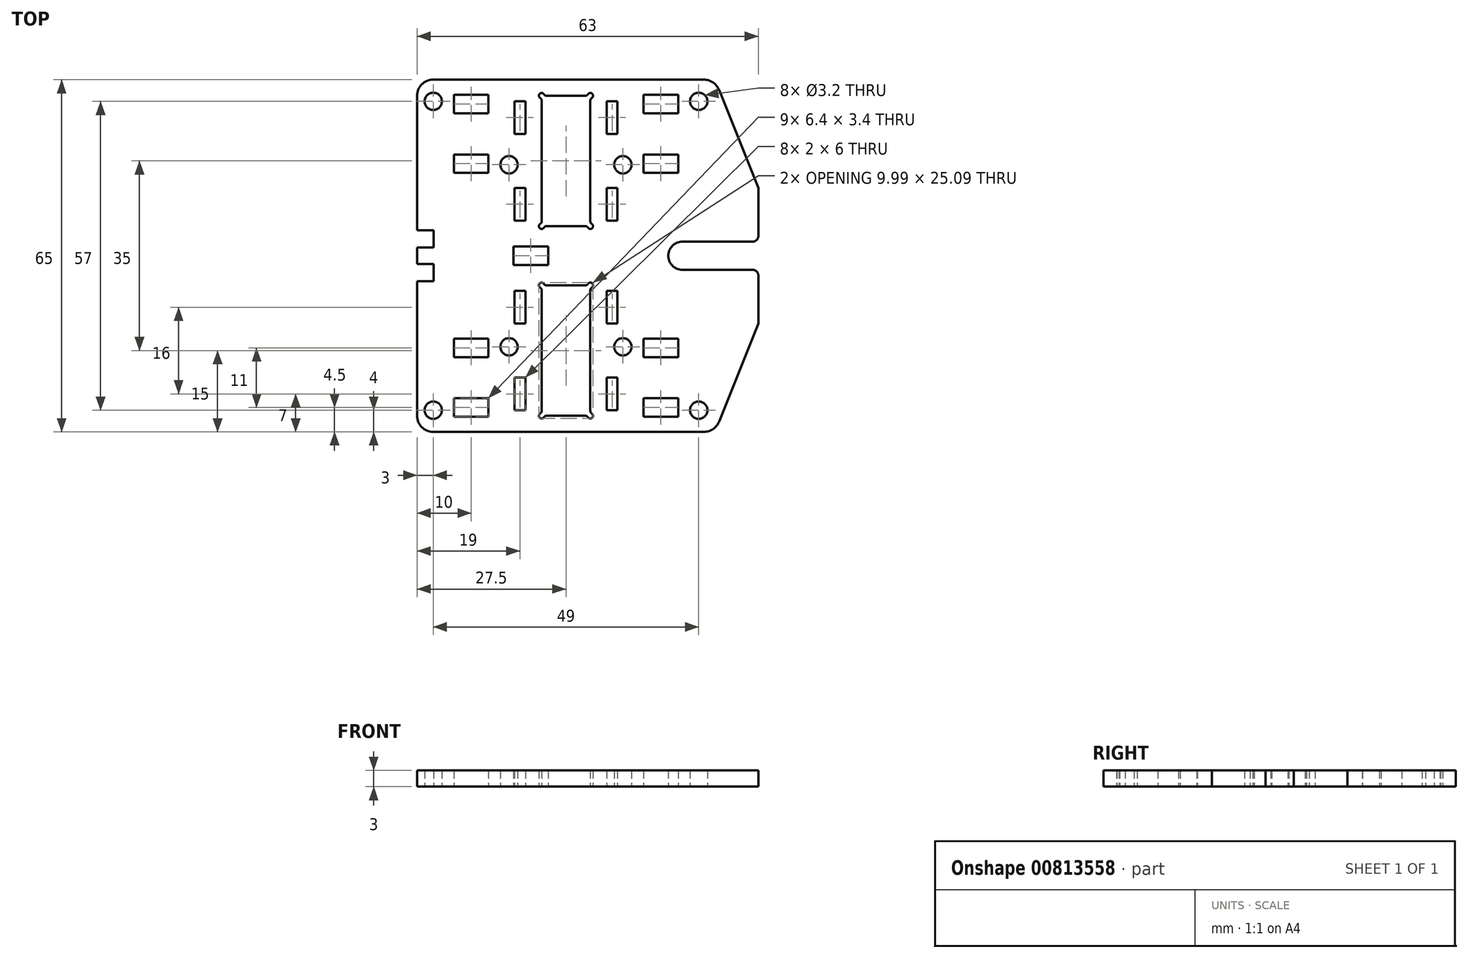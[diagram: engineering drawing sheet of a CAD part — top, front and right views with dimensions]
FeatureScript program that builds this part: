
annotation { "Feature Type Name" : "Feature", "Feature Type Description" : "" }
export const myFeature = defineFeature(function(context is Context, id is Id, definition is map)
    precondition{}
    {
        {
            var Q0;
            Q0=qCreatedBy(makeId("Top.planeOp"),FACE);
            var sketch = newSketch(context, id + "F0", { "sketchPlane" : qUnion([Q0])});
            skLineSegment(sketch, "E0", {"start": v(-31.5, -1.5) * mm, "end": v(-31.5, 1.5) * mm});
            skArc(sketch, "E1", {"start": v(-8.75, -29.12) * mm, "mid": v(-8.85, -29.9) * mm, "end": v(-8.07, -29.8) * mm});
            skArc(sketch, "E2", {"start": v(-7.63, -29.55) * mm, "mid": v(-7.88, -29.62) * mm, "end": v(-8.07, -29.8) * mm});
            skArc(sketch, "E3", {"start": v(-8.75, -29.12) * mm, "mid": v(-8.57, -28.93) * mm, "end": v(-8.5, -28.68) * mm});
            skLineSegment(sketch, "E4", {"start": v(-8.5, -6.32) * mm, "end": v(-8.5, -28.68) * mm});
            skArc(sketch, "E5", {"start": v(-8.5, -6.32) * mm, "mid": v(-8.57, -6.07) * mm, "end": v(-8.75, -5.88) * mm});
            skArc(sketch, "E6", {"start": v(-8.07, -5.2) * mm, "mid": v(-8.85, -5.1) * mm, "end": v(-8.75, -5.88) * mm});
            skArc(sketch, "E7", {"start": v(-8.07, -5.2) * mm, "mid": v(-7.88, -5.38) * mm, "end": v(-7.63, -5.45) * mm});
            skLineSegment(sketch, "E8", {"start": v(-0.37, -5.45) * mm, "end": v(-7.63, -5.45) * mm});
            skArc(sketch, "E9", {"start": v(-0.37, -5.45) * mm, "mid": v(-0.12, -5.38) * mm, "end": v(0.07, -5.2) * mm});
            skArc(sketch, "E10", {"start": v(0.75, -5.88) * mm, "mid": v(0.85, -5.1) * mm, "end": v(0.07, -5.2) * mm});
            skArc(sketch, "E11", {"start": v(0.75, -5.88) * mm, "mid": v(0.57, -6.07) * mm, "end": v(0.5, -6.32) * mm});
            skLineSegment(sketch, "E12", {"start": v(0.5, -28.68) * mm, "end": v(0.5, -6.32) * mm});
            skArc(sketch, "E13", {"start": v(0.5, -28.68) * mm, "mid": v(0.57, -28.93) * mm, "end": v(0.75, -29.12) * mm});
            skArc(sketch, "E14", {"start": v(0.07, -29.8) * mm, "mid": v(0.85, -29.9) * mm, "end": v(0.75, -29.12) * mm});
            skArc(sketch, "E15", {"start": v(0.07, -29.8) * mm, "mid": v(-0.12, -29.62) * mm, "end": v(-0.37, -29.55) * mm});
            skLineSegment(sketch, "E16", {"start": v(-7.63, -29.55) * mm, "end": v(-0.37, -29.55) * mm});
            skArc(sketch, "E17", {"start": v(-8.75, 5.88) * mm, "mid": v(-8.85, 5.1) * mm, "end": v(-8.07, 5.2) * mm});
            skArc(sketch, "E18", {"start": v(-7.63, 5.45) * mm, "mid": v(-7.88, 5.38) * mm, "end": v(-8.07, 5.2) * mm});
            skArc(sketch, "E19", {"start": v(-8.75, 5.88) * mm, "mid": v(-8.57, 6.07) * mm, "end": v(-8.5, 6.32) * mm});
            skLineSegment(sketch, "E20", {"start": v(-8.5, 28.68) * mm, "end": v(-8.5, 6.32) * mm});
            skArc(sketch, "E21", {"start": v(-8.5, 28.68) * mm, "mid": v(-8.57, 28.93) * mm, "end": v(-8.75, 29.12) * mm});
            skArc(sketch, "E22", {"start": v(-8.07, 29.8) * mm, "mid": v(-8.85, 29.9) * mm, "end": v(-8.75, 29.12) * mm});
            skArc(sketch, "E23", {"start": v(-8.07, 29.8) * mm, "mid": v(-7.88, 29.62) * mm, "end": v(-7.63, 29.55) * mm});
            skLineSegment(sketch, "E24", {"start": v(-0.37, 29.55) * mm, "end": v(-7.63, 29.55) * mm});
            skArc(sketch, "E25", {"start": v(-0.37, 29.55) * mm, "mid": v(-0.12, 29.62) * mm, "end": v(0.07, 29.8) * mm});
            skArc(sketch, "E26", {"start": v(0.75, 29.12) * mm, "mid": v(0.85, 29.9) * mm, "end": v(0.07, 29.8) * mm});
            skArc(sketch, "E27", {"start": v(0.75, 29.12) * mm, "mid": v(0.57, 28.93) * mm, "end": v(0.5, 28.68) * mm});
            skLineSegment(sketch, "E28", {"start": v(0.5, 6.32) * mm, "end": v(0.5, 28.68) * mm});
            skArc(sketch, "E29", {"start": v(0.5, 6.32) * mm, "mid": v(0.57, 6.07) * mm, "end": v(0.75, 5.88) * mm});
            skArc(sketch, "E30", {"start": v(0.07, 5.2) * mm, "mid": v(0.85, 5.1) * mm, "end": v(0.75, 5.88) * mm});
            skArc(sketch, "E31", {"start": v(0.07, 5.2) * mm, "mid": v(-0.12, 5.38) * mm, "end": v(-0.37, 5.45) * mm});
            skLineSegment(sketch, "E32", {"start": v(-7.63, 5.45) * mm, "end": v(-0.37, 5.45) * mm});
            skLineSegment(sketch, "E33", {"start": v(-31.5, -4.7) * mm, "end": v(-28.4, -4.7) * mm});
            skLineSegment(sketch, "E34", {"start": v(-28.4, -1.5) * mm, "end": v(-31.5, -1.5) * mm});
            skLineSegment(sketch, "E35", {"start": v(-28.4, -4.7) * mm, "end": v(-28.4, -1.5) * mm});
            skLineSegment(sketch, "E36", {"start": v(-31.5, 1.5) * mm, "end": v(-28.4, 1.5) * mm});
            skLineSegment(sketch, "E37", {"start": v(-28.4, 4.7) * mm, "end": v(-31.5, 4.7) * mm});
            skLineSegment(sketch, "E38", {"start": v(-28.4, 1.5) * mm, "end": v(-28.4, 4.7) * mm});
            skLineSegment(sketch, "E39", {"start": v(-13.7, 1.7) * mm, "end": v(-13.7, -1.7) * mm});
            skLineSegment(sketch, "E40", {"start": v(-13.7, -1.7) * mm, "end": v(-7.3, -1.7) * mm});
            skLineSegment(sketch, "E41", {"start": v(-13.7, 1.7) * mm, "end": v(-7.3, 1.7) * mm});
            skLineSegment(sketch, "E42", {"start": v(-7.3, -1.7) * mm, "end": v(-7.3, 1.7) * mm});
            skLineSegment(sketch, "E43", {"start": v(3.5, -12.5) * mm, "end": v(5.5, -12.5) * mm});
            skLineSegment(sketch, "E44", {"start": v(-13.5, -12.5) * mm, "end": v(-11.5, -12.5) * mm});
            skLineSegment(sketch, "E45", {"start": v(5.5, 12.5) * mm, "end": v(3.5, 12.5) * mm});
            skLineSegment(sketch, "E46", {"start": v(-11.5, 12.5) * mm, "end": v(-13.5, 12.5) * mm});
            skLineSegment(sketch, "E47", {"start": v(3.5, 22.5) * mm, "end": v(5.5, 22.5) * mm});
            skLineSegment(sketch, "E48", {"start": v(-13.5, 22.5) * mm, "end": v(-11.5, 22.5) * mm});
            skLineSegment(sketch, "E49", {"start": v(5.5, -22.5) * mm, "end": v(3.5, -22.5) * mm});
            skLineSegment(sketch, "E50", {"start": v(-11.5, -22.5) * mm, "end": v(-13.5, -22.5) * mm});
            skLineSegment(sketch, "E51", {"start": v(-13.5, -28.5) * mm, "end": v(-11.5, -28.5) * mm});
            skLineSegment(sketch, "E52", {"start": v(-11.5, -6.5) * mm, "end": v(-13.5, -6.5) * mm});
            skLineSegment(sketch, "E53", {"start": v(-13.5, 6.5) * mm, "end": v(-11.5, 6.5) * mm});
            skLineSegment(sketch, "E54", {"start": v(-11.5, 28.5) * mm, "end": v(-13.5, 28.5) * mm});
            skLineSegment(sketch, "E55", {"start": v(3.5, -28.5) * mm, "end": v(5.5, -28.5) * mm});
            skLineSegment(sketch, "E56", {"start": v(5.5, -6.5) * mm, "end": v(3.5, -6.5) * mm});
            skLineSegment(sketch, "E57", {"start": v(3.5, 6.5) * mm, "end": v(5.5, 6.5) * mm});
            skLineSegment(sketch, "E58", {"start": v(5.5, 28.5) * mm, "end": v(3.5, 28.5) * mm});
            skLineSegment(sketch, "E59", {"start": v(-13.5, -22.5) * mm, "end": v(-13.5, -28.5) * mm});
            skLineSegment(sketch, "E60", {"start": v(-11.5, -28.5) * mm, "end": v(-11.5, -22.5) * mm});
            skLineSegment(sketch, "E61", {"start": v(-13.5, -6.5) * mm, "end": v(-13.5, -12.5) * mm});
            skLineSegment(sketch, "E62", {"start": v(-11.5, -12.5) * mm, "end": v(-11.5, -6.5) * mm});
            skLineSegment(sketch, "E63", {"start": v(-13.5, 12.5) * mm, "end": v(-13.5, 6.5) * mm});
            skLineSegment(sketch, "E64", {"start": v(-11.5, 6.5) * mm, "end": v(-11.5, 12.5) * mm});
            skLineSegment(sketch, "E65", {"start": v(-13.5, 28.5) * mm, "end": v(-13.5, 22.5) * mm});
            skLineSegment(sketch, "E66", {"start": v(-11.5, 22.5) * mm, "end": v(-11.5, 28.5) * mm});
            skLineSegment(sketch, "E67", {"start": v(3.5, -22.5) * mm, "end": v(3.5, -28.5) * mm});
            skLineSegment(sketch, "E68", {"start": v(5.5, -28.5) * mm, "end": v(5.5, -22.5) * mm});
            skLineSegment(sketch, "E69", {"start": v(3.5, -6.5) * mm, "end": v(3.5, -12.5) * mm});
            skLineSegment(sketch, "E70", {"start": v(5.5, -12.5) * mm, "end": v(5.5, -6.5) * mm});
            skLineSegment(sketch, "E71", {"start": v(3.5, 12.5) * mm, "end": v(3.5, 6.5) * mm});
            skLineSegment(sketch, "E72", {"start": v(5.5, 6.5) * mm, "end": v(5.5, 12.5) * mm});
            skLineSegment(sketch, "E73", {"start": v(3.5, 28.5) * mm, "end": v(3.5, 22.5) * mm});
            skLineSegment(sketch, "E74", {"start": v(5.5, 22.5) * mm, "end": v(5.5, 28.5) * mm});
            skArc(sketch, "E75", {"start": v(17.5, 2.6) * mm, "mid": v(14.9, 0) * mm, "end": v(17.5, -2.6) * mm});
            skLineSegment(sketch, "E76", {"start": v(31.5, 12.5) * mm, "end": v(31.5, 3.6) * mm});
            skLineSegment(sketch, "E77", {"start": v(17.5, 2.6) * mm, "end": v(30.5, 2.6) * mm});
            skArc(sketch, "E78", {"start": v(30.5, 2.6) * mm, "mid": v(31.2, 2.9) * mm, "end": v(31.5, 3.6) * mm});
            skLineSegment(sketch, "E79", {"start": v(17.5, -2.6) * mm, "end": v(30.5, -2.6) * mm});
            skLineSegment(sketch, "E80", {"start": v(31.5, -12.5) * mm, "end": v(31.5, -3.6) * mm});
            skArc(sketch, "E81", {"start": v(31.5, -3.6) * mm, "mid": v(31.2, -2.9) * mm, "end": v(30.5, -2.6) * mm});
            skLineSegment(sketch, "E82", {"start": v(10.3, -26.3) * mm, "end": v(10.3, -29.7) * mm});
            skLineSegment(sketch, "E83", {"start": v(10.3, -29.7) * mm, "end": v(16.7, -29.7) * mm});
            skLineSegment(sketch, "E84", {"start": v(10.3, -26.3) * mm, "end": v(16.7, -26.3) * mm});
            skLineSegment(sketch, "E85", {"start": v(16.7, -29.7) * mm, "end": v(16.7, -26.3) * mm});
            skLineSegment(sketch, "E86", {"start": v(10.3, -15.3) * mm, "end": v(10.3, -18.7) * mm});
            skLineSegment(sketch, "E87", {"start": v(10.3, -18.7) * mm, "end": v(16.7, -18.7) * mm});
            skLineSegment(sketch, "E88", {"start": v(10.3, -15.3) * mm, "end": v(16.7, -15.3) * mm});
            skLineSegment(sketch, "E89", {"start": v(16.7, -18.7) * mm, "end": v(16.7, -15.3) * mm});
            skLineSegment(sketch, "E90", {"start": v(10.3, 18.7) * mm, "end": v(10.3, 15.3) * mm});
            skLineSegment(sketch, "E91", {"start": v(10.3, 15.3) * mm, "end": v(16.7, 15.3) * mm});
            skLineSegment(sketch, "E92", {"start": v(10.3, 18.7) * mm, "end": v(16.7, 18.7) * mm});
            skLineSegment(sketch, "E93", {"start": v(16.7, 15.3) * mm, "end": v(16.7, 18.7) * mm});
            skLineSegment(sketch, "E94", {"start": v(10.3, 29.7) * mm, "end": v(10.3, 26.3) * mm});
            skLineSegment(sketch, "E95", {"start": v(10.3, 26.3) * mm, "end": v(16.7, 26.3) * mm});
            skLineSegment(sketch, "E96", {"start": v(10.3, 29.7) * mm, "end": v(16.7, 29.7) * mm});
            skLineSegment(sketch, "E97", {"start": v(16.7, 26.3) * mm, "end": v(16.7, 29.7) * mm});
            skCircle(sketch, "E98", {"center": v(20.5, -28.5) * mm, "radius": 1.6 * mm});
            skCircle(sketch, "E99", {"center": v(20.5, 28.5) * mm, "radius": 1.6 * mm});
            skLineSegment(sketch, "E100", {"start": v(-24.7, -26.3) * mm, "end": v(-24.7, -29.7) * mm});
            skLineSegment(sketch, "E101", {"start": v(-24.7, -29.7) * mm, "end": v(-18.3, -29.7) * mm});
            skLineSegment(sketch, "E102", {"start": v(-24.7, -26.3) * mm, "end": v(-18.3, -26.3) * mm});
            skLineSegment(sketch, "E103", {"start": v(-18.3, -29.7) * mm, "end": v(-18.3, -26.3) * mm});
            skLineSegment(sketch, "E104", {"start": v(-24.7, -15.3) * mm, "end": v(-24.7, -18.7) * mm});
            skLineSegment(sketch, "E105", {"start": v(-24.7, -18.7) * mm, "end": v(-18.3, -18.7) * mm});
            skLineSegment(sketch, "E106", {"start": v(-24.7, -15.3) * mm, "end": v(-18.3, -15.3) * mm});
            skLineSegment(sketch, "E107", {"start": v(-18.3, -18.7) * mm, "end": v(-18.3, -15.3) * mm});
            skLineSegment(sketch, "E108", {"start": v(-24.7, 18.7) * mm, "end": v(-24.7, 15.3) * mm});
            skLineSegment(sketch, "E109", {"start": v(-24.7, 15.3) * mm, "end": v(-18.3, 15.3) * mm});
            skLineSegment(sketch, "E110", {"start": v(-24.7, 18.7) * mm, "end": v(-18.3, 18.7) * mm});
            skLineSegment(sketch, "E111", {"start": v(-18.3, 15.3) * mm, "end": v(-18.3, 18.7) * mm});
            skLineSegment(sketch, "E112", {"start": v(-24.7, 29.7) * mm, "end": v(-24.7, 26.3) * mm});
            skLineSegment(sketch, "E113", {"start": v(-24.7, 26.3) * mm, "end": v(-18.3, 26.3) * mm});
            skLineSegment(sketch, "E114", {"start": v(-24.7, 29.7) * mm, "end": v(-18.3, 29.7) * mm});
            skLineSegment(sketch, "E115", {"start": v(-18.3, 26.3) * mm, "end": v(-18.3, 29.7) * mm});
            skCircle(sketch, "E116", {"center": v(-28.5, -28.5) * mm, "radius": 1.6 * mm});
            skCircle(sketch, "E117", {"center": v(-28.5, 28.5) * mm, "radius": 1.6 * mm});
            skCircle(sketch, "E118", {"center": v(-14.5, -16.8) * mm, "radius": 1.6 * mm});
            skCircle(sketch, "E119", {"center": v(6.5, -16.8) * mm, "radius": 1.6 * mm});
            skCircle(sketch, "E120", {"center": v(6.5, 16.8) * mm, "radius": 1.6 * mm});
            skCircle(sketch, "E121", {"center": v(-14.5, 16.8) * mm, "radius": 1.6 * mm});
            skArc(sketch, "E122", {"start": v(24.25, 30.61) * mm, "mid": v(23.15, 31.98) * mm, "end": v(21.47, 32.5) * mm});
            skLineSegment(sketch, "E123", {"start": v(31.5, -12.5) * mm, "end": v(24.25, -30.61) * mm});
            skArc(sketch, "E124", {"start": v(21.47, -32.5) * mm, "mid": v(23.15, -31.98) * mm, "end": v(24.25, -30.61) * mm});
            skLineSegment(sketch, "E125", {"start": v(-31.5, -29.5) * mm, "end": v(-31.5, -4.7) * mm});
            skLineSegment(sketch, "E126", {"start": v(21.47, -32.5) * mm, "end": v(-28.5, -32.5) * mm});
            skArc(sketch, "E127", {"start": v(-31.5, -29.5) * mm, "mid": v(-30.62, -31.62) * mm, "end": v(-28.5, -32.5) * mm});
            skLineSegment(sketch, "E128", {"start": v(-31.5, 4.7) * mm, "end": v(-31.5, 29.5) * mm});
            skLineSegment(sketch, "E129", {"start": v(21.47, 32.5) * mm, "end": v(-28.5, 32.5) * mm});
            skArc(sketch, "E130", {"start": v(-28.5, 32.5) * mm, "mid": v(-30.62, 31.62) * mm, "end": v(-31.5, 29.5) * mm});
            skLineSegment(sketch, "E131", {"start": v(24.25, 30.61) * mm, "end": v(31.5, 12.5) * mm});
            skSolve(sketch);
        }
        {
            var Q0;
            Q0=qSketchRegion(id+"F0",true);
            extrude(context, id + "F1", {"entities" : qUnion([Q0]), "depth" : 3 * mm, "offsetDistance" : 25 * mm});
        }
        {
            var Q0;
            Q0=makeQuery(id+"F1.opExtrude","CAP_EDGE",EDGE,{"disambiguationData":[OSD([sQuery(id+"F0.wireOp",EDGE,"E20")])],"isStart":false});
            cPoint(context, id + "F2", {"entities" : qUnion([Q0]), "parameter" : 0.5});
        }
        {
            var Q0;
            Q0=qCreatedBy(id+"F2",VERTEX);
            var Q1;
            Q1=makeQuery(id+"F1.opExtrude","CAP_EDGE",EDGE,{"disambiguationData":[OSD([sQuery(id+"F0.wireOp",EDGE,"E20")])],"isStart":false});
            cPlane(context, id + "F3", {"entities" : qUnion([Q0, Q1]), "cplaneType" : CPlaneType.LINE_POINT, "offset" : 25 * mm, "width" : 150 * mm, "height" : 150 * mm});
        }
        {
            var Q0;
            Q0=qCreatedBy(id+"F3.planeOp",FACE);
            var sketch = newSketch(context, id + "F4", { "sketchPlane" : qUnion([Q0])});
            skCircle(sketch, "E132", {"center": v(-4, 9) * mm, "radius": 7.5 * mm, "construction": true});
            skSolve(sketch);
        }
        {
            var Q0;
            Q0=makeQuery(id+"F1.opExtrude","CAP_EDGE",EDGE,{"disambiguationData":[OSD([sQuery(id+"F0.wireOp",EDGE,"E12")])],"isStart":false});
            cPoint(context, id + "F5", {"entities" : qUnion([Q0]), "parameter" : 0.5});
        }
        {
            var Q0;
            Q0=qCreatedBy(id+"F5",VERTEX);
            var Q1;
            Q1=makeQuery(id+"F1.opExtrude","CAP_EDGE",EDGE,{"disambiguationData":[OSD([sQuery(id+"F0.wireOp",EDGE,"E12")])],"isStart":false});
            cPlane(context, id + "F6", {"entities" : qUnion([Q0, Q1]), "cplaneType" : CPlaneType.LINE_POINT, "offset" : 25 * mm, "width" : 150 * mm, "height" : 150 * mm});
        }
        {
            var Q0;
            Q0=qCreatedBy(id+"F6.planeOp",FACE);
            var sketch = newSketch(context, id + "F7", { "sketchPlane" : qUnion([Q0])});
            skCircle(sketch, "E133.0", {"center": v(4, 9) * mm, "radius": 7.5 * mm, "construction": true});
            skSolve(sketch);
        }
    });
